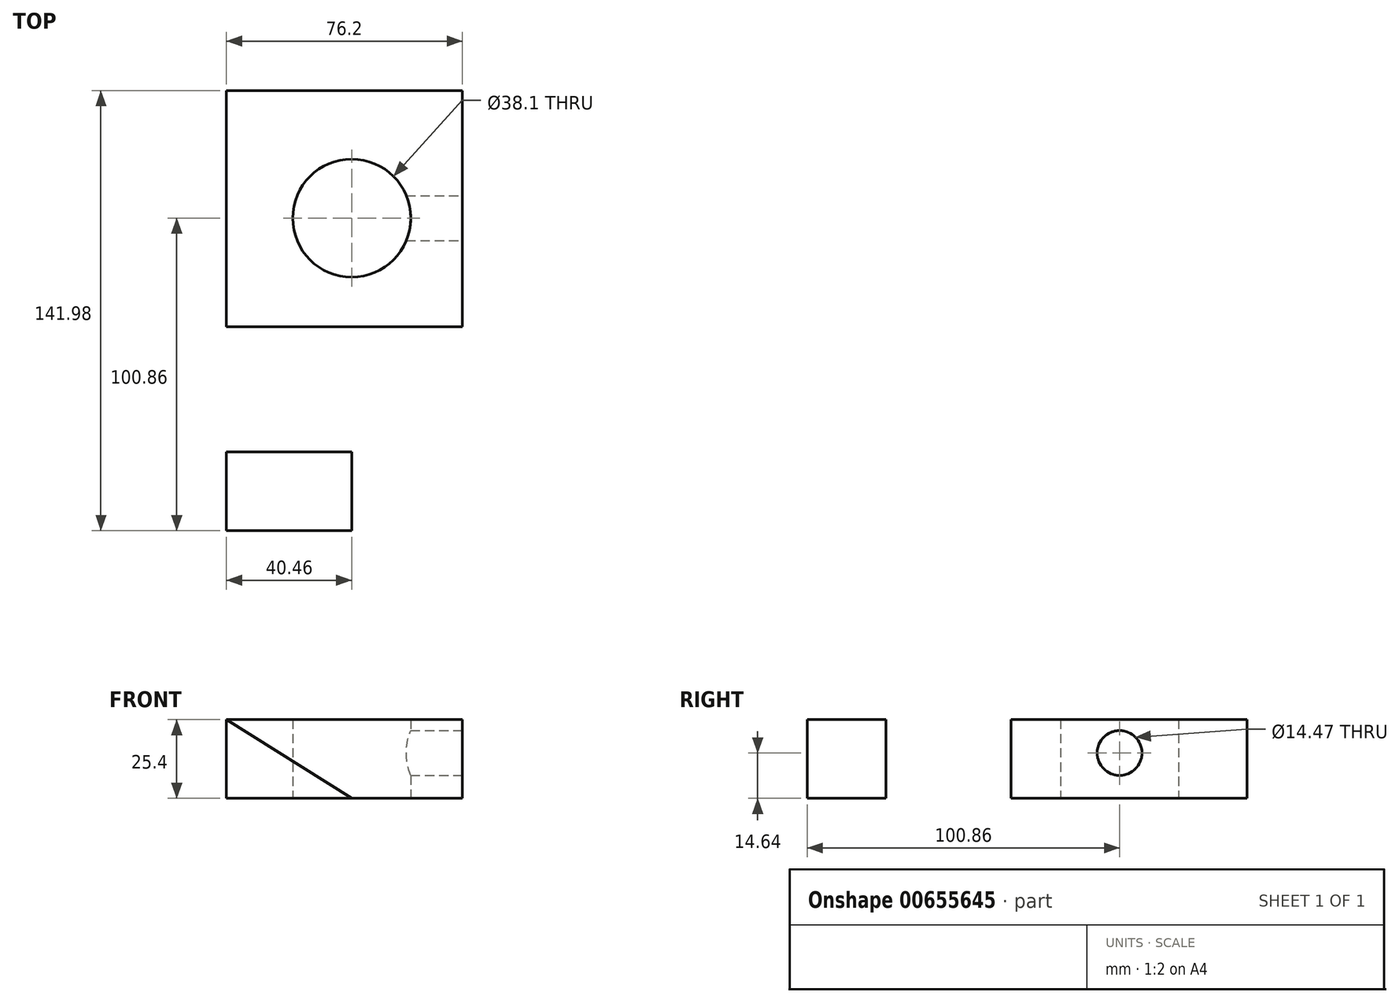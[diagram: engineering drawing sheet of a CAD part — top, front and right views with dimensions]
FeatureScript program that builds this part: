
annotation { "Feature Type Name" : "Feature", "Feature Type Description" : "" }
export const myFeature = defineFeature(function(context is Context, id is Id, definition is map)
    precondition{}
    {
        {
            var Q0;
            Q0=qCreatedBy(makeId("Top.planeOp"),FACE);
            var sketch = newSketch(context, id + "F0", { "sketchPlane" : qUnion([Q0])});
            skLineSegment(sketch, "E0.bottom", {"start": v(-40.46, 41.12) * mm, "end": v(35.74, 41.12) * mm});
            skLineSegment(sketch, "E0.top", {"start": v(-40.46, -35.08) * mm, "end": v(35.74, -35.08) * mm});
            skLineSegment(sketch, "E0.left", {"start": v(-40.46, 41.12) * mm, "end": v(-40.46, -35.08) * mm});
            skLineSegment(sketch, "E0.right", {"start": v(35.74, 41.12) * mm, "end": v(35.74, -35.08) * mm});
            skCircle(sketch, "E1", {"center": v(0, 0) * mm, "radius": 19.05 * mm});
            skSolve(sketch);
        }
        {
            var Q0;
            Q0=makeQuery(id+"F0.imprint","IMPRINT",FACE,{"disambiguationData":[TD([[makeQuery(id+"F0.imprint","IMPRINT",EDGE,{"derivedFrom":sQuery(id+"F0.wireOp",EDGE,"E0.bottom")}),-1.0]])]});
            extrude(context, id + "F1", {"entities" : qUnion([Q0]), "depth" : 25.4 * mm, "offsetDistance" : 25.4 * mm});
        }
        {
            var Q0;
            Q0=makeQuery(id+"F1.opExtrude","SWEPT_FACE",FACE,{"disambiguationData":[OSD([sQuery(id+"F0.wireOp",EDGE,"E0.right")])]});
            var sketch = newSketch(context, id + "F2", { "sketchPlane" : qUnion([Q0])});
            skCircle(sketch, "E2", {"center": v(0, 14.64) * mm, "radius": 7.23 * mm});
            skSolve(sketch);
        }
        {
            var Q0;
            Q0=makeQuery(id+"F2.imprint","IMPRINT",FACE,{"disambiguationData":[TD([[makeQuery(id+"F2.imprint","IMPRINT",EDGE,{"derivedFrom":sQuery(id+"F2.wireOp",EDGE,"E2")}),1.0]])]});
            extrude(context, id + "F3", {"entities" : qUnion([Q0]), "operationType" : NewBodyOperationType.REMOVE, "oppositeDirection" : true, "depth" : 25.4 * mm, "offsetDistance" : 25.4 * mm});
        }
        {
            var Q0;
            Q0=makeQuery(id+"F1.opExtrude","SWEPT_FACE",FACE,{"disambiguationData":[OSD([sQuery(id+"F0.wireOp",EDGE,"E0.top")])]});
            cPlane(context, id + "F4", {"entities" : qUnion([Q0]), "cplaneType" : CPlaneType.OFFSET, "offset" : 40.4 * mm, "width" : 152.4 * mm, "height" : 152.4 * mm});
        }
        {
            var Q0;
            Q0=makeQuery(id+"F1.opExtrude","SWEPT_FACE",FACE,{"disambiguationData":[OSD([sQuery(id+"F0.wireOp",EDGE,"E0.top")])]});
            var sketch = newSketch(context, id + "F5", { "sketchPlane" : qUnion([Q0])});
            skPoint(sketch, "E3.0", {"position": v(-40.46, 25.4) * mm});
            skLineSegment(sketch, "E4", {"start": v(-40.46, 25.4) * mm, "end": v(0, 0) * mm});
            skSolve(sketch);
        }
        {
            var Q0;
            Q0=qCreatedBy(id+"F4.planeOp",FACE);
            var sketch = newSketch(context, id + "F6", { "sketchPlane" : qUnion([Q0])});
            skLineSegment(sketch, "E5.0.0", {"start": v(0, 0) * mm, "end": v(-40.46, 25.4) * mm});
            skLineSegment(sketch, "E5.0.1", {"start": v(-40.46, 25.4) * mm, "end": v(-40.46, 0) * mm});
            skLineSegment(sketch, "E5.0.2", {"start": v(-40.46, 0) * mm, "end": v(0, 0) * mm});
            skSolve(sketch);
        }
        {
            var Q0;
            Q0=makeQuery(id+"F6.imprint","IMPRINT",FACE,{"disambiguationData":[TD([[makeQuery(id+"F6.imprint","IMPRINT",EDGE,{"derivedFrom":sQuery(id+"F6.wireOp",EDGE,"E5.0.0")}),1.0]])]});
            extrude(context, id + "F7", {"entities" : qUnion([Q0]), "depth" : 25.4 * mm, "offsetDistance" : 25.4 * mm});
        }
    });
